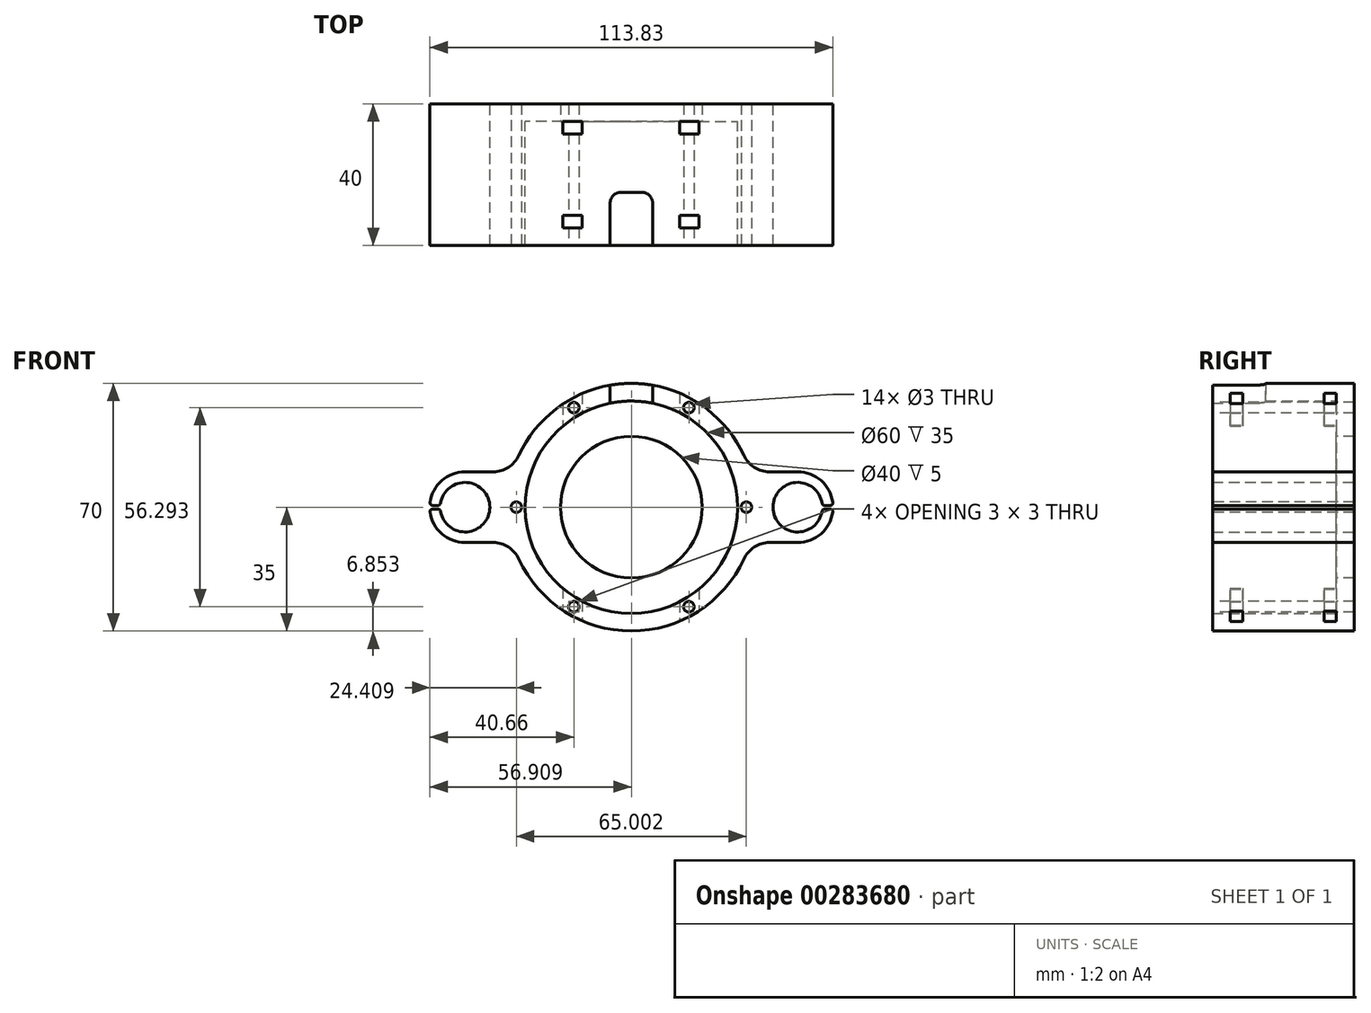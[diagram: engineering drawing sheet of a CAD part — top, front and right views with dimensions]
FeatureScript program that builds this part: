
annotation { "Feature Type Name" : "Feature", "Feature Type Description" : "" }
export const myFeature = defineFeature(function(context is Context, id is Id, definition is map)
    precondition{}
    {
        {
            var Q0;
            Q0=qCreatedBy(makeId("Front.planeOp"),FACE);
            var sketch = newSketch(context, id + "F0", { "sketchPlane" : qUnion([Q0])});
            skArc(sketch, "E0", {"start": v(-42.32, -0.5) * mm, "mid": v(-28.34, 0) * mm, "end": v(-42.32, 0.5) * mm});
            skArc(sketch, "E1", {"start": v(65.64, 0.5) * mm, "mid": v(51.66, 0) * mm, "end": v(65.64, -0.5) * mm});
            skArc(sketch, "E2", {"start": v(-35.34, 10) * mm, "mid": v(-42.23, 7.25) * mm, "end": v(-45.33, 0.5) * mm});
            skArc(sketch, "E3", {"start": v(58.66, -10) * mm, "mid": v(65.55, -7.25) * mm, "end": v(68.65, -0.5) * mm});
            skLineSegment(sketch, "E4", {"start": v(-35.34, 10) * mm, "end": v(-27.4, 10) * mm});
            skLineSegment(sketch, "E5", {"start": v(-35.34, -10) * mm, "end": v(-27.4, -10) * mm});
            skPoint(sketch, "E6", {"position": v(11.66, 0) * mm});
            skCircle(sketch, "E7", {"center": v(11.66, 0) * mm, "radius": 30 * mm});
            skArc(sketch, "E8", {"start": v(43.44, 14.65) * mm, "mid": v(11.66, 35) * mm, "end": v(-20.13, 14.65) * mm});
            skLineSegment(sketch, "E9.trimOffspring", {"start": v(50.71, 10) * mm, "end": v(58.66, 10) * mm});
            skLineSegment(sketch, "E10.trimOffspring", {"start": v(50.71, -10) * mm, "end": v(58.66, -10) * mm});
            skArc(sketch, "E11.trimOffspring", {"start": v(-20.13, -14.65) * mm, "mid": v(11.66, -35) * mm, "end": v(43.44, -14.65) * mm});
            skPoint(sketch, "E12.visualSharp", {"position": v(-21.88, 10) * mm});
            skArc(sketch, "E12.filletArc", {"start": v(-27.4, 10) * mm, "mid": v(-23.08, 11.26) * mm, "end": v(-20.13, 14.65) * mm});
            skPoint(sketch, "E13.visualSharp", {"position": v(-21.88, -10) * mm});
            skArc(sketch, "E13.filletArc", {"start": v(-20.13, -14.65) * mm, "mid": v(-23.08, -11.26) * mm, "end": v(-27.4, -10) * mm});
            skPoint(sketch, "E14.visualSharp", {"position": v(45.2, -10) * mm});
            skArc(sketch, "E14.filletArc", {"start": v(50.71, -10) * mm, "mid": v(46.4, -11.26) * mm, "end": v(43.44, -14.65) * mm});
            skPoint(sketch, "E15.visualSharp", {"position": v(45.2, 10) * mm});
            skArc(sketch, "E15.filletArc", {"start": v(43.44, 14.65) * mm, "mid": v(46.4, 11.26) * mm, "end": v(50.71, 10) * mm});
            skCircle(sketch, "E16", {"center": v(11.66, 0) * mm, "radius": 20 * mm});
            skLineSegment(sketch, "E17", {"start": v(-45.33, 0.5) * mm, "end": v(-42.32, 0.5) * mm});
            skLineSegment(sketch, "E18", {"start": v(-42.32, -0.5) * mm, "end": v(-45.33, -0.5) * mm});
            skArc(sketch, "E19.trimOffspring", {"start": v(-45.33, -0.5) * mm, "mid": v(-42.23, -7.25) * mm, "end": v(-35.34, -10) * mm});
            skLineSegment(sketch, "E20", {"start": v(68.65, 0.5) * mm, "end": v(65.64, 0.5) * mm});
            skLineSegment(sketch, "E21", {"start": v(68.65, -0.5) * mm, "end": v(65.64, -0.5) * mm});
            skArc(sketch, "E22.trimOffspring", {"start": v(68.65, 0.5) * mm, "mid": v(65.55, 7.25) * mm, "end": v(58.66, 10) * mm});
            skSolve(sketch);
        }
        {
            var Q0;
            Q0=makeQuery(id+"F0.imprint","IMPRINT",FACE,{"disambiguationData":[TD([[makeQuery(id+"F0.imprint","IMPRINT",EDGE,{"derivedFrom":sQuery(id+"F0.wireOp",EDGE,"E0")}),-1.0]])]});
            extrude(context, id + "F1", {"entities" : qUnion([Q0]), "depth" : 35 * mm});
        }
        {
            var Q0;
            Q0=makeQuery(id+"F0.imprint","IMPRINT",FACE,{"disambiguationData":[TD([[makeQuery(id+"F0.imprint","IMPRINT",EDGE,{"derivedFrom":sQuery(id+"F0.wireOp",EDGE,"E7")}),1.0]])]});
            var Q1;
            Q1=makeQuery(id+"F0.imprint","IMPRINT",FACE,{"disambiguationData":[TD([[makeQuery(id+"F0.imprint","IMPRINT",EDGE,{"derivedFrom":sQuery(id+"F0.wireOp",EDGE,"E0")}),-1.0]])]});
            extrude(context, id + "F2", {"entities" : qUnion([Q0, Q1]), "operationType" : NewBodyOperationType.ADD, "oppositeDirection" : true, "depth" : 5 * mm});
        }
        {
            var Q0;
            Q0=qCreatedBy(makeId("Front.planeOp"),FACE);
            cPlane(context, id + "F3", {"entities" : qUnion([Q0]), "cplaneType" : CPlaneType.OFFSET, "offset" : 35 * mm, "width" : 150 * mm, "height" : 150 * mm});
        }
        {
            var Q0;
            Q0=qCreatedBy(id+"F3.planeOp",FACE);
            var sketch = newSketch(context, id + "F4", { "sketchPlane" : qUnion([Q0])});
            skPoint(sketch, "E23", {"position": v(-20.84, 0) * mm});
            skPoint(sketch, "E24.1.0", {"position": v(-4.6, 28.15) * mm});
            skPoint(sketch, "E24.2.0", {"position": v(27.91, 28.15) * mm});
            skPoint(sketch, "E24.3.0", {"position": v(44.16, 0) * mm});
            skPoint(sketch, "E24.4.0", {"position": v(27.91, -28.15) * mm});
            skPoint(sketch, "E24.5.0", {"position": v(-4.6, -28.15) * mm});
            skPoint(sketch, "E24.center", {"position": v(11.66, 0) * mm});
            skLineSegment(sketch, "E24.anchor1", {"start": v(11.66, 0) * mm, "end": v(-20.84, 0) * mm, "construction": true});
            skLineSegment(sketch, "E24.anchor2", {"start": v(11.66, 0) * mm, "end": v(-4.6, -28.15) * mm, "construction": true});
            skLineSegment(sketch, "E25", {"start": v(5.66, 37.5) * mm, "end": v(5.66, 26.85) * mm});
            skLineSegment(sketch, "E26", {"start": v(5.66, 26.85) * mm, "end": v(17.66, 26.85) * mm});
            skLineSegment(sketch, "E27", {"start": v(17.66, 26.85) * mm, "end": v(17.66, 37.5) * mm});
            skLineSegment(sketch, "E28", {"start": v(17.66, 37.5) * mm, "end": v(5.66, 37.5) * mm});
            skSolve(sketch);
        }
        {
            var Q0;
            Q0=sQuery(id+"F4.wireOp",VERTEX,"E24.1.0");
            var Q1;
            Q1=sQuery(id+"F4.wireOp",VERTEX,"E24.2.0");
            var Q2;
            Q2=sQuery(id+"F4.wireOp",VERTEX,"E24.3.0");
            var Q3;
            Q3=sQuery(id+"F4.wireOp",VERTEX,"E24.4.0");
            var Q4;
            Q4=sQuery(id+"F4.wireOp",VERTEX,"E24.5.0");
            var Q5;
            Q5=sQuery(id+"F4.wireOp",VERTEX,"E23");
            var Q6;
            Q6=makeQuery(id+"F1.opExtrude","SWEPT_BODY",BODY,{"disambiguationData":[OSD([sQuery(id+"F0.wireOp",EDGE,"E0"),sQuery(id+"F0.wireOp",EDGE,"E1"),sQuery(id+"F0.wireOp",EDGE,"E2"),sQuery(id+"F0.wireOp",EDGE,"E3"),sQuery(id+"F0.wireOp",EDGE,"E4"),sQuery(id+"F0.wireOp",EDGE,"E5"),sQuery(id+"F0.wireOp",EDGE,"E7"),sQuery(id+"F0.wireOp",EDGE,"E8"),sQuery(id+"F0.wireOp",EDGE,"E9.trimOffspring"),sQuery(id+"F0.wireOp",EDGE,"E10.trimOffspring"),sQuery(id+"F0.wireOp",EDGE,"E11.trimOffspring"),sQuery(id+"F0.wireOp",EDGE,"E12.filletArc"),sQuery(id+"F0.wireOp",EDGE,"E13.filletArc"),sQuery(id+"F0.wireOp",EDGE,"E14.filletArc"),sQuery(id+"F0.wireOp",EDGE,"E15.filletArc")])]});
            hole(context, id + "F5", {"style" : HoleStyle.SIMPLE, "endStyle" : HoleEndStyle.THROUGH, "holeDiameter" : 3 * mm, "tappedDepth" : 12 * mm, "tapClearance" : 3, "startFromSketch" : true, "locations" : qUnion([Q0, Q1, Q2, Q3, Q4, Q5]), "scope" : qUnion([Q6])});
        }
        {
            var Q0;
            Q0=makeQuery(id+"F4.imprint","IMPRINT",FACE,{"disambiguationData":[TD([[makeQuery(id+"F4.imprint","IMPRINT",EDGE,{"derivedFrom":sQuery(id+"F4.wireOp",EDGE,"E25")}),1.0]])]});
            extrude(context, id + "F6", {"entities" : qUnion([Q0]), "operationType" : NewBodyOperationType.REMOVE, "oppositeDirection" : true, "depth" : 15 * mm});
        }
        {
            var Q0;
            Q0=makeQuery(id+"F6.boolean.opBoolean","COPY",EDGE,{"derivedFrom":makeQuery(id+"F6.opExtrude","CAP_EDGE",EDGE,{"disambiguationData":[OSD([sQuery(id+"F4.wireOp",EDGE,"E25")])],"isStart":false})});
            var Q1;
            Q1=makeQuery(id+"F6.boolean.opBoolean","COPY",EDGE,{"derivedFrom":makeQuery(id+"F6.opExtrude","CAP_EDGE",EDGE,{"disambiguationData":[OSD([sQuery(id+"F4.wireOp",EDGE,"E27")])],"isStart":false})});
            var Q2;
            Q2=makeQuery(id+"F6.boolean.opBoolean","COPY",EDGE,{"derivedFrom":makeQuery(id+"F6.opExtrude","CAP_EDGE",EDGE,{"disambiguationData":[OSD([sQuery(id+"F4.wireOp",EDGE,"E25")])],"isStart":true})});
            var Q3;
            Q3=makeQuery(id+"F6.boolean.opBoolean","COPY",EDGE,{"derivedFrom":makeQuery(id+"F6.opExtrude","CAP_EDGE",EDGE,{"disambiguationData":[OSD([sQuery(id+"F4.wireOp",EDGE,"E27")])],"isStart":true})});
            fillet(context, id + "F7", {"entities" : qUnion([Q0, Q1, Q2, Q3]), "radius" : 3 * mm, "tangentPropagation" : true, "allowEdgeOverflow" : false});
        }
        {
            var Q0;
            {var subQ0=sQuery(id+"F0.wireOp",EDGE,"E22.trimOffspring");var subQ1=sQuery(id+"F0.wireOp",EDGE,"E20");Q0=makeQuery(id+"F2.boolean.opBoolean","MERGE",EDGE,{"derivedFrom":[makeQuery(id+"F1.opExtrude","SWEPT_EDGE",EDGE,{"disambiguationData":[OSD([subQ1,subQ0])]}),makeQuery(id+"F2.opExtrude","SWEPT_EDGE",EDGE,{"disambiguationData":[OSD([subQ1,subQ0])]})]});}
            var Q1;
            {var subQ0=sQuery(id+"F0.wireOp",EDGE,"E21");var subQ1=sQuery(id+"F0.wireOp",EDGE,"E3");Q1=makeQuery(id+"F2.boolean.opBoolean","MERGE",EDGE,{"derivedFrom":[makeQuery(id+"F1.opExtrude","SWEPT_EDGE",EDGE,{"disambiguationData":[OSD([subQ1,subQ0])]}),makeQuery(id+"F2.opExtrude","SWEPT_EDGE",EDGE,{"disambiguationData":[OSD([subQ1,subQ0])]})]});}
            var Q2;
            {var subQ0=sQuery(id+"F0.wireOp",EDGE,"E21");var subQ1=sQuery(id+"F0.wireOp",EDGE,"E1");Q2=makeQuery(id+"F2.boolean.opBoolean","MERGE",EDGE,{"derivedFrom":[makeQuery(id+"F1.opExtrude","SWEPT_EDGE",EDGE,{"disambiguationData":[OSD([subQ1,subQ0])]}),makeQuery(id+"F2.opExtrude","SWEPT_EDGE",EDGE,{"disambiguationData":[OSD([subQ1,subQ0])]})]});}
            var Q3;
            {var subQ0=sQuery(id+"F0.wireOp",EDGE,"E20");var subQ1=sQuery(id+"F0.wireOp",EDGE,"E1");Q3=makeQuery(id+"F2.boolean.opBoolean","MERGE",EDGE,{"derivedFrom":[makeQuery(id+"F1.opExtrude","SWEPT_EDGE",EDGE,{"disambiguationData":[OSD([subQ1,subQ0])]}),makeQuery(id+"F2.opExtrude","SWEPT_EDGE",EDGE,{"disambiguationData":[OSD([subQ1,subQ0])]})]});}
            fillet(context, id + "F8", {"entities" : qUnion([Q0, Q1, Q2, Q3]), "radius" : 0.7 * mm, "tangentPropagation" : true, "allowEdgeOverflow" : false});
        }
        {
            var Q0;
            {var subQ0=sQuery(id+"F0.wireOp",EDGE,"E17");var subQ1=sQuery(id+"F0.wireOp",EDGE,"E0");Q0=makeQuery(id+"F2.boolean.opBoolean","MERGE",EDGE,{"derivedFrom":[makeQuery(id+"F1.opExtrude","SWEPT_EDGE",EDGE,{"disambiguationData":[OSD([subQ1,subQ0])]}),makeQuery(id+"F2.opExtrude","SWEPT_EDGE",EDGE,{"disambiguationData":[OSD([subQ1,subQ0])]})]});}
            var Q1;
            {var subQ0=sQuery(id+"F0.wireOp",EDGE,"E18");var subQ1=sQuery(id+"F0.wireOp",EDGE,"E0");Q1=makeQuery(id+"F2.boolean.opBoolean","MERGE",EDGE,{"derivedFrom":[makeQuery(id+"F1.opExtrude","SWEPT_EDGE",EDGE,{"disambiguationData":[OSD([subQ1,subQ0])]}),makeQuery(id+"F2.opExtrude","SWEPT_EDGE",EDGE,{"disambiguationData":[OSD([subQ1,subQ0])]})]});}
            var Q2;
            {var subQ0=sQuery(id+"F0.wireOp",EDGE,"E17");var subQ1=sQuery(id+"F0.wireOp",EDGE,"E2");Q2=makeQuery(id+"F2.boolean.opBoolean","MERGE",EDGE,{"derivedFrom":[makeQuery(id+"F1.opExtrude","SWEPT_EDGE",EDGE,{"disambiguationData":[OSD([subQ1,subQ0])]}),makeQuery(id+"F2.opExtrude","SWEPT_EDGE",EDGE,{"disambiguationData":[OSD([subQ1,subQ0])]})]});}
            var Q3;
            {var subQ0=sQuery(id+"F0.wireOp",EDGE,"E19.trimOffspring");var subQ1=sQuery(id+"F0.wireOp",EDGE,"E18");Q3=makeQuery(id+"F2.boolean.opBoolean","MERGE",EDGE,{"derivedFrom":[makeQuery(id+"F1.opExtrude","SWEPT_EDGE",EDGE,{"disambiguationData":[OSD([subQ1,subQ0])]}),makeQuery(id+"F2.opExtrude","SWEPT_EDGE",EDGE,{"disambiguationData":[OSD([subQ1,subQ0])]})]});}
            fillet(context, id + "F9", {"entities" : qUnion([Q0, Q1, Q2, Q3]), "radius" : 0.8 * mm, "tangentPropagation" : true, "allowEdgeOverflow" : false});
        }
        {
            var Q0;
            Q0=qCreatedBy(makeId("Top.planeOp"),FACE);
            var sketch = newSketch(context, id + "F10", { "sketchPlane" : qUnion([Q0])});
            skPoint(sketch, "E29", {"position": v(-5, -27) * mm});
            skPoint(sketch, "E30", {"position": v(28, -27) * mm});
            skPoint(sketch, "E31", {"position": v(-5, -28.63) * mm});
            skLineSegment(sketch, "E32.bottom", {"start": v(-7.75, -26.5) * mm, "end": v(-2.25, -26.5) * mm});
            skLineSegment(sketch, "E32.top", {"start": v(-7.75, -30) * mm, "end": v(-2.25, -30) * mm});
            skLineSegment(sketch, "E32.left", {"start": v(-7.75, -26.5) * mm, "end": v(-7.75, -30) * mm});
            skLineSegment(sketch, "E32.right", {"start": v(-2.25, -26.5) * mm, "end": v(-2.25, -30) * mm});
            skPoint(sketch, "E33", {"position": v(28, -28.63) * mm});
            skLineSegment(sketch, "E34.bottom", {"start": v(25.25, -26.5) * mm, "end": v(30.75, -26.5) * mm});
            skLineSegment(sketch, "E34.top", {"start": v(25.25, -30) * mm, "end": v(30.75, -30) * mm});
            skLineSegment(sketch, "E34.left", {"start": v(25.25, -26.5) * mm, "end": v(25.25, -30) * mm});
            skLineSegment(sketch, "E34.right", {"start": v(30.75, -26.5) * mm, "end": v(30.75, -30) * mm});
            skPoint(sketch, "E35", {"position": v(-5, -3.3) * mm});
            skPoint(sketch, "E36", {"position": v(28, -3.3) * mm});
            skPoint(sketch, "E37", {"position": v(-5, -4.93) * mm});
            skLineSegment(sketch, "E38.bottom", {"start": v(-7.75, 0) * mm, "end": v(-2.25, 0) * mm});
            skLineSegment(sketch, "E38.top", {"start": v(-7.75, -3.5) * mm, "end": v(-2.25, -3.5) * mm});
            skLineSegment(sketch, "E38.left", {"start": v(-7.75, 0) * mm, "end": v(-7.75, -3.5) * mm});
            skLineSegment(sketch, "E38.right", {"start": v(-2.25, 0) * mm, "end": v(-2.25, -3.5) * mm});
            skPoint(sketch, "E39", {"position": v(28, -2.13) * mm});
            skLineSegment(sketch, "E40.bottom", {"start": v(25.25, 0) * mm, "end": v(30.75, 0) * mm});
            skLineSegment(sketch, "E40.top", {"start": v(25.25, -3.5) * mm, "end": v(30.75, -3.5) * mm});
            skLineSegment(sketch, "E40.left", {"start": v(25.25, 0) * mm, "end": v(25.25, -3.5) * mm});
            skLineSegment(sketch, "E40.right", {"start": v(30.75, 0) * mm, "end": v(30.75, -3.5) * mm});
            skSolve(sketch);
        }
        {
            var Q0;
            Q0=makeQuery(id+"F10.imprint","IMPRINT",FACE,{"disambiguationData":[TD([[makeQuery(id+"F10.imprint","IMPRINT",EDGE,{"derivedFrom":sQuery(id+"F10.wireOp",EDGE,"E32.bottom")}),-1.0]])]});
            var Q1;
            Q1=makeQuery(id+"F10.imprint","IMPRINT",FACE,{"disambiguationData":[TD([[makeQuery(id+"F10.imprint","IMPRINT",EDGE,{"derivedFrom":sQuery(id+"F10.wireOp",EDGE,"E34.bottom")}),-1.0]])]});
            var Q2;
            Q2=makeQuery(id+"F10.imprint","IMPRINT",FACE,{"disambiguationData":[TD([[makeQuery(id+"F10.imprint","IMPRINT",EDGE,{"derivedFrom":sQuery(id+"F10.wireOp",EDGE,"E38.bottom")}),-1.0]])]});
            var Q3;
            Q3=makeQuery(id+"F10.imprint","IMPRINT",FACE,{"disambiguationData":[TD([[makeQuery(id+"F10.imprint","IMPRINT",EDGE,{"derivedFrom":sQuery(id+"F10.wireOp",EDGE,"E40.bottom")}),-1.0]])]});
            extrude(context, id + "F11", {"entities" : qUnion([Q0, Q1, Q2, Q3]), "operationType" : NewBodyOperationType.REMOVE, "depth" : 50 * mm, "hasSecondDirection" : true, "secondDirectionOppositeDirection" : true, "secondDirectionDepth" : 50 * mm});
        }
    });
